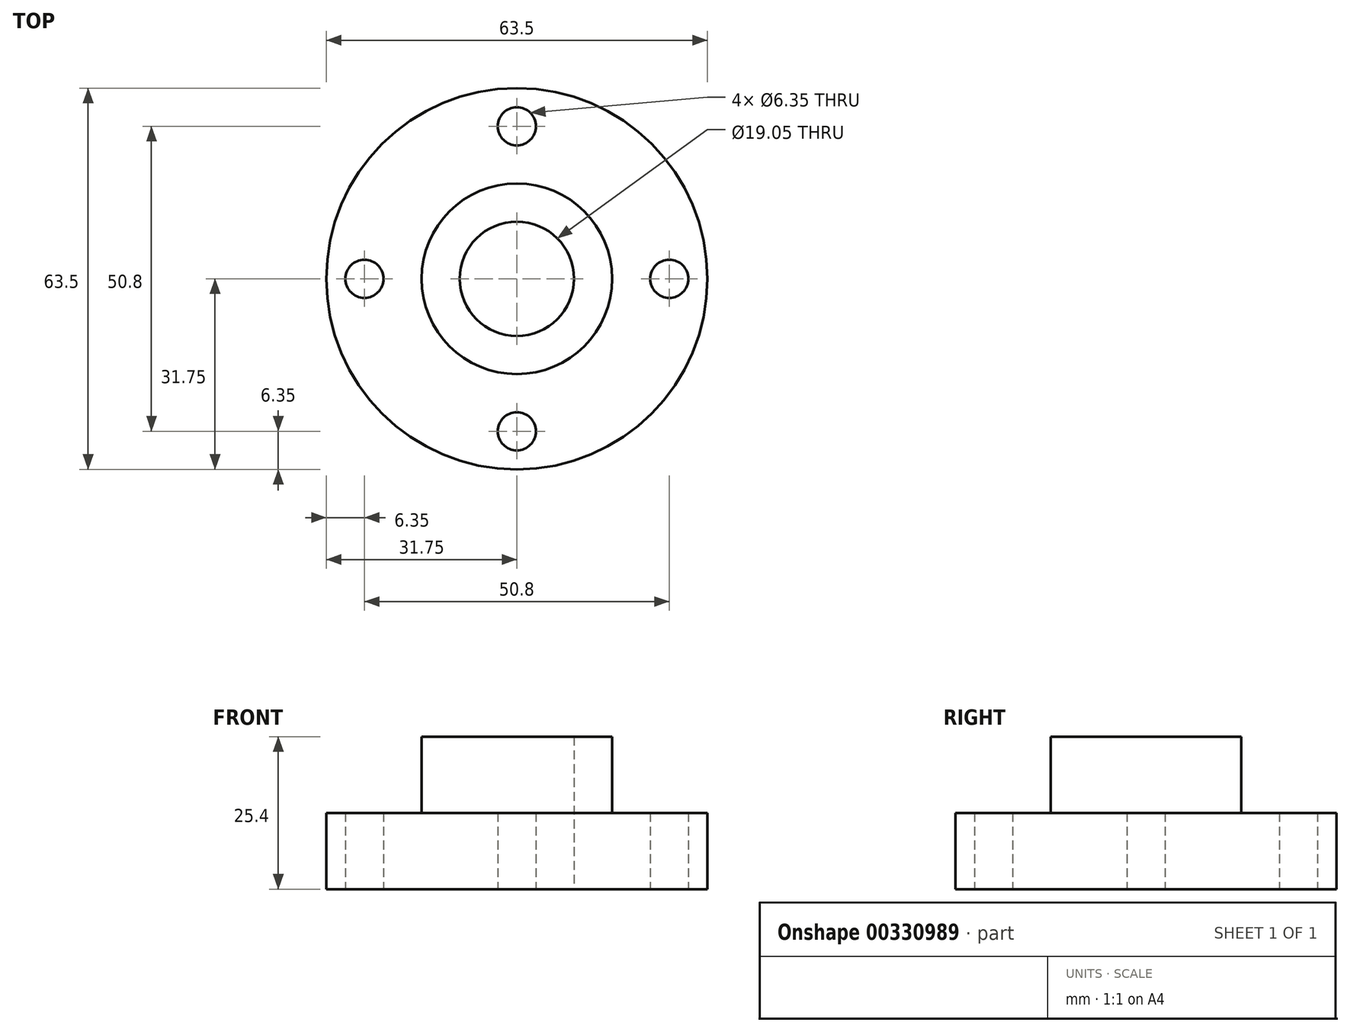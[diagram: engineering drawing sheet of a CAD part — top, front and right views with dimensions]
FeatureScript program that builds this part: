
annotation { "Feature Type Name" : "Feature", "Feature Type Description" : "" }
export const myFeature = defineFeature(function(context is Context, id is Id, definition is map)
    precondition{}
    {
        {
            var Q0;
            Q0=qCreatedBy(makeId("Top.planeOp"),FACE);
            var sketch = newSketch(context, id + "F0", { "sketchPlane" : qUnion([Q0])});
            skCircle(sketch, "E0", {"center": v(0, 0) * mm, "radius": 31.75 * mm});
            skCircle(sketch, "E1", {"center": v(0, 0) * mm, "radius": 25.4 * mm, "construction": true});
            skCircle(sketch, "E2", {"center": v(0, 0) * mm, "radius": 15.88 * mm});
            skCircle(sketch, "E3", {"center": v(0, 0) * mm, "radius": 9.53 * mm});
            skPoint(sketch, "E4", {"position": v(0, 25.4) * mm});
            skPoint(sketch, "E5", {"position": v(25.4, 0) * mm});
            skPoint(sketch, "E6", {"position": v(0, -25.4) * mm});
            skPoint(sketch, "E7", {"position": v(-25.4, 0) * mm});
            skCircle(sketch, "E8", {"center": v(0, 25.4) * mm, "radius": 3.18 * mm});
            skCircle(sketch, "E9", {"center": v(-25.4, 0) * mm, "radius": 3.18 * mm});
            skCircle(sketch, "E10", {"center": v(0, -25.4) * mm, "radius": 3.18 * mm});
            skCircle(sketch, "E11", {"center": v(25.4, 0) * mm, "radius": 3.18 * mm});
            skSolve(sketch);
        }
        {
            var Q0;
            Q0=makeQuery(id+"F0.imprint","IMPRINT",FACE,{"disambiguationData":[TD([[makeQuery(id+"F0.imprint","IMPRINT",EDGE,{"derivedFrom":sQuery(id+"F0.wireOp",EDGE,"E0")}),1.0]])]});
            extrude(context, id + "F1", {"entities" : qUnion([Q0]), "depth" : 12.7 * mm});
        }
        {
            var Q0;
            Q0=makeQuery(id+"F0.imprint","IMPRINT",FACE,{"disambiguationData":[TD([[makeQuery(id+"F0.imprint","IMPRINT",EDGE,{"derivedFrom":sQuery(id+"F0.wireOp",EDGE,"E2")}),1.0]])]});
            extrude(context, id + "F2", {"entities" : qUnion([Q0]), "operationType" : NewBodyOperationType.ADD, "depth" : 25.4 * mm});
        }
    });
